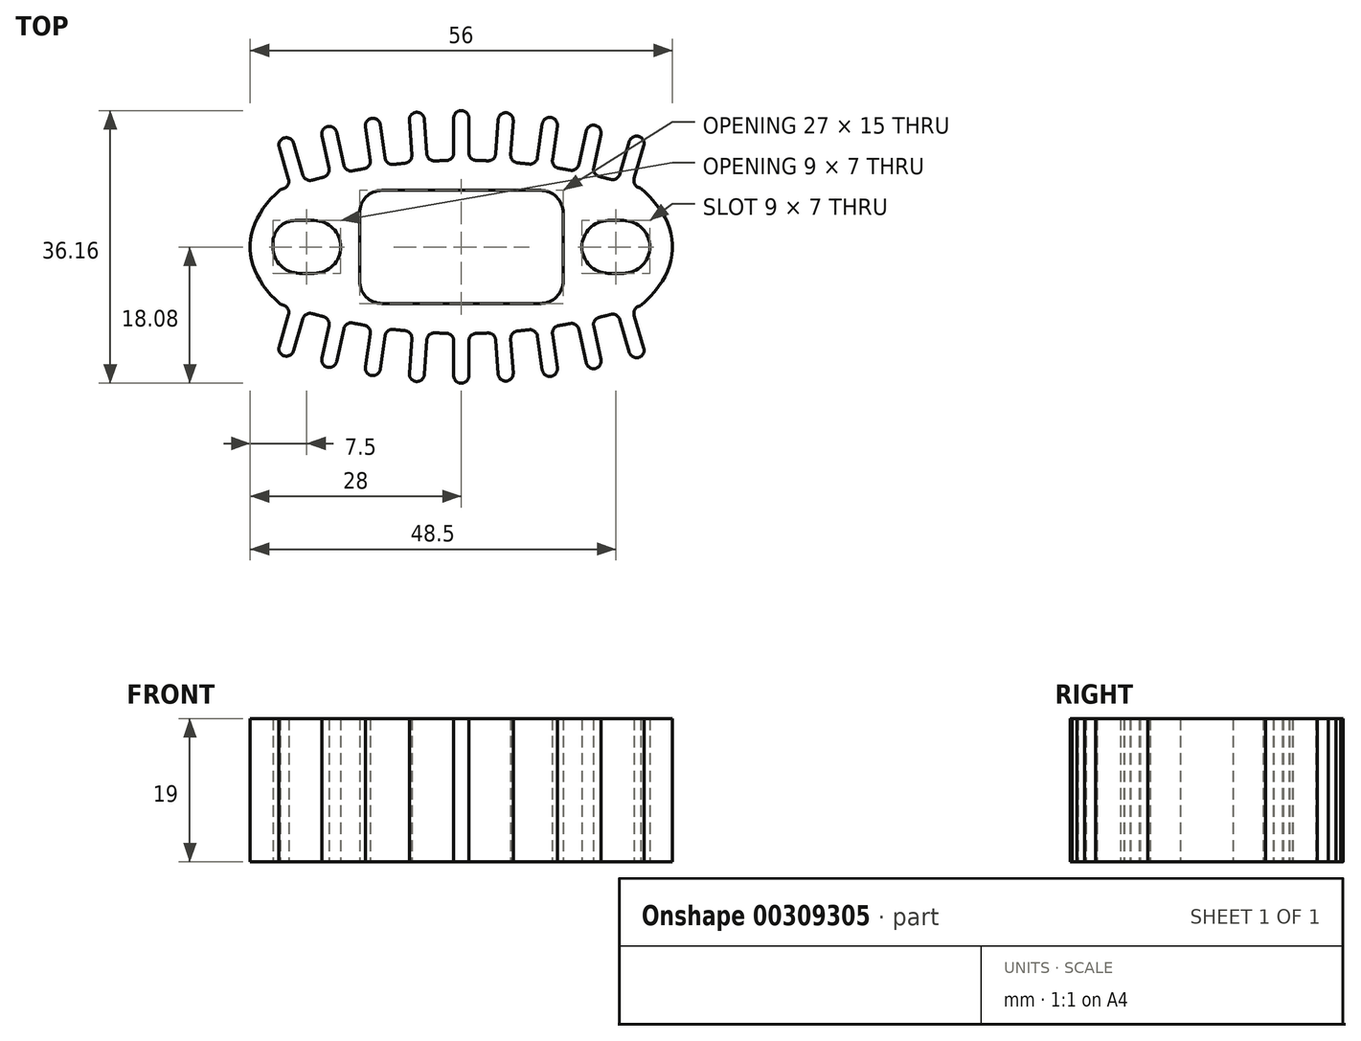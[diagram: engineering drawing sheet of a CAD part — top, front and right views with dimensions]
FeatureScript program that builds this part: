
annotation { "Feature Type Name" : "Feature", "Feature Type Description" : "" }
export const myFeature = defineFeature(function(context is Context, id is Id, definition is map)
    precondition{}
    {
        {
            var Q0;
            Q0=qCreatedBy(makeId("Top.planeOp"),FACE);
            var sketch = newSketch(context, id + "F0", { "sketchPlane" : qUnion([Q0])});
            skLineSegment(sketch, "E0.bottom", {"start": v(-10.5, 7.5) * mm, "end": v(10.5, 7.5) * mm});
            skLineSegment(sketch, "E0.top", {"start": v(-10.5, -7.5) * mm, "end": v(10.5, -7.5) * mm});
            skLineSegment(sketch, "E0.left", {"start": v(-13.5, 4.5) * mm, "end": v(-13.5, -4.5) * mm});
            skLineSegment(sketch, "E0.right", {"start": v(13.5, 4.5) * mm, "end": v(13.5, -4.5) * mm});
            skPoint(sketch, "E1.visualSharp", {"position": v(-13.5, 7.5) * mm});
            skArc(sketch, "E1.filletArc", {"start": v(-10.5, 7.5) * mm, "mid": v(-12.62, 6.62) * mm, "end": v(-13.5, 4.5) * mm});
            skPoint(sketch, "E2.visualSharp", {"position": v(-13.5, -7.5) * mm});
            skArc(sketch, "E2.filletArc", {"start": v(-13.5, -4.5) * mm, "mid": v(-12.62, -6.62) * mm, "end": v(-10.5, -7.5) * mm});
            skPoint(sketch, "E3.visualSharp", {"position": v(13.5, -7.5) * mm});
            skArc(sketch, "E3.filletArc", {"start": v(10.5, -7.5) * mm, "mid": v(12.62, -6.62) * mm, "end": v(13.5, -4.5) * mm});
            skPoint(sketch, "E4.visualSharp", {"position": v(13.5, 7.5) * mm});
            skArc(sketch, "E4.filletArc", {"start": v(13.5, 4.5) * mm, "mid": v(12.62, 6.62) * mm, "end": v(10.5, 7.5) * mm});
            skLineSegment(sketch, "E5.bottom", {"start": v(-22, 3.5) * mm, "end": v(-19.5, 3.5) * mm});
            skLineSegment(sketch, "E5.top", {"start": v(-21.5, -3.5) * mm, "end": v(-19.5, -3.5) * mm});
            skLineSegment(sketch, "E5.left", {"start": v(-25, 0.5) * mm, "end": v(-25, 0) * mm});
            skLineSegment(sketch, "E5.right", {"start": v(-16, 0) * mm, "end": v(-16, 0) * mm});
            skLineSegment(sketch, "E6.bottom", {"start": v(19.5, 3.5) * mm, "end": v(21.5, 3.5) * mm});
            skLineSegment(sketch, "E6.top", {"start": v(19.5, -3.5) * mm, "end": v(21.5, -3.5) * mm});
            skLineSegment(sketch, "E6.left", {"start": v(16, 0) * mm, "end": v(16, 0) * mm});
            skLineSegment(sketch, "E6.right", {"start": v(25, 0) * mm, "end": v(25, 0) * mm});
            skPoint(sketch, "E7.visualSharp", {"position": v(-25, 3.5) * mm});
            skArc(sketch, "E7.filletArc", {"start": v(-22, 3.5) * mm, "mid": v(-24.12, 2.62) * mm, "end": v(-25, 0.5) * mm});
            skPoint(sketch, "E8.visualSharp", {"position": v(-25, -3.5) * mm});
            skArc(sketch, "E8.filletArc", {"start": v(-25, 0) * mm, "mid": v(-23.97, -2.47) * mm, "end": v(-21.5, -3.5) * mm});
            skPoint(sketch, "E9.visualSharp", {"position": v(-16, -3.5) * mm});
            skArc(sketch, "E9.filletArc", {"start": v(-19.5, -3.5) * mm, "mid": v(-17.03, -2.47) * mm, "end": v(-16, 0) * mm});
            skPoint(sketch, "E10.visualSharp", {"position": v(-16, 3.5) * mm});
            skArc(sketch, "E10.filletArc", {"start": v(-16, 0) * mm, "mid": v(-17.03, 2.47) * mm, "end": v(-19.5, 3.5) * mm});
            skPoint(sketch, "E11.visualSharp", {"position": v(16, -3.5) * mm});
            skArc(sketch, "E11.filletArc", {"start": v(16, 0) * mm, "mid": v(17.03, -2.47) * mm, "end": v(19.5, -3.5) * mm});
            skPoint(sketch, "E12.visualSharp", {"position": v(16, 3.5) * mm});
            skArc(sketch, "E12.filletArc", {"start": v(19.5, 3.5) * mm, "mid": v(17.03, 2.47) * mm, "end": v(16, 0) * mm});
            skPoint(sketch, "E13.visualSharp", {"position": v(25, -3.5) * mm});
            skArc(sketch, "E13.filletArc", {"start": v(21.5, -3.5) * mm, "mid": v(23.97, -2.47) * mm, "end": v(25, 0) * mm});
            skPoint(sketch, "E14.visualSharp", {"position": v(25, 3.5) * mm});
            skArc(sketch, "E14.filletArc", {"start": v(25, 0) * mm, "mid": v(23.97, 2.47) * mm, "end": v(21.5, 3.5) * mm});
            skEllipticalArc(sketch, "E15", {});
            skArc(sketch, "E16", {"start": v(23.77, 7.8) * mm, "mid": v(23.68, 7.83) * mm, "end": v(23.59, 7.86) * mm});
            skLineSegment(sketch, "E17.0", {"start": v(23.52, 14.67) * mm, "end": v(23.52, 14.67) * mm});
            skEllipticalArc(sketch, "E18.trimOffspring", {});
            skPoint(sketch, "E19", {"position": v(-28, 0) * mm});
            skLineSegment(sketch, "E20.0", {"start": v(1, 12.47) * mm, "end": v(1, 17.08) * mm});
            skLineSegment(sketch, "E21.MirrorCS", {"start": v(-1, 12.46) * mm, "end": v(-1, 17.08) * mm});
            skLineSegment(sketch, "E22.1.0", {"start": v(-6.57, 12.18) * mm, "end": v(-6.9, 16.79) * mm});
            skLineSegment(sketch, "E22.1.1", {"start": v(-4.57, 12.33) * mm, "end": v(-4.9, 16.93) * mm});
            skLineSegment(sketch, "E22.2.0", {"start": v(-12.1, 11.5) * mm, "end": v(-12.73, 15.93) * mm});
            skLineSegment(sketch, "E22.2.1", {"start": v(-10.11, 11.8) * mm, "end": v(-10.75, 16.22) * mm});
            skLineSegment(sketch, "E22.3.0", {"start": v(-17.55, 10.42) * mm, "end": v(-18.5, 14.78) * mm});
            skLineSegment(sketch, "E22.3.1", {"start": v(-15.6, 10.86) * mm, "end": v(-16.55, 15.2) * mm});
            skLineSegment(sketch, "E22.4.0", {"start": v(-22.92, 8.96) * mm, "end": v(-24.17, 13.21) * mm});
            skLineSegment(sketch, "E22.4.1", {"start": v(-21, 9.54) * mm, "end": v(-22.25, 13.78) * mm});
            skLineSegment(sketch, "E22.84.0", {"start": v(21, 9.64) * mm, "end": v(22.29, 14) * mm});
            skLineSegment(sketch, "E22.84.1", {"start": v(22.93, 9.1) * mm, "end": v(24.2, 13.43) * mm});
            skLineSegment(sketch, "E22.85.0", {"start": v(15.6, 10.94) * mm, "end": v(16.56, 15.36) * mm});
            skLineSegment(sketch, "E22.85.1", {"start": v(17.55, 10.52) * mm, "end": v(18.51, 14.94) * mm});
            skLineSegment(sketch, "E22.86.0", {"start": v(10.1, 11.84) * mm, "end": v(10.75, 16.32) * mm});
            skLineSegment(sketch, "E22.86.1", {"start": v(12.08, 11.57) * mm, "end": v(12.73, 16.04) * mm});
            skLineSegment(sketch, "E22.87.0", {"start": v(4.56, 12.35) * mm, "end": v(4.88, 16.87) * mm});
            skLineSegment(sketch, "E22.87.1", {"start": v(6.55, 12.22) * mm, "end": v(6.88, 16.73) * mm});
            skLineSegment(sketch, "E23.trimOffspring", {"start": v(-11.89, 17.06) * mm, "end": v(-11.89, 17.06) * mm});
            skLineSegment(sketch, "E24.trimOffspring", {"start": v(-23.5, 14.45) * mm, "end": v(-23.5, 14.45) * mm});
            skPoint(sketch, "E25.orphan", {"position": v(-25.73, 13.75) * mm});
            skLineSegment(sketch, "E26.trimOffspring", {"start": v(-17.74, 15.96) * mm, "end": v(-17.74, 15.96) * mm});
            skLineSegment(sketch, "E27.trimOffspring", {"start": v(5.95, 17.8) * mm, "end": v(5.95, 17.8) * mm});
            skLineSegment(sketch, "E28.trimOffspring", {"start": v(11.88, 17.17) * mm, "end": v(11.88, 17.17) * mm});
            skLineSegment(sketch, "E29.trimOffspring", {"start": v(17.74, 16.13) * mm, "end": v(17.74, 16.13) * mm});
            skPoint(sketch, "E30.orphan", {"position": v(25.8, 13.97) * mm});
            skPoint(sketch, "E31.orphan", {"position": v(-4.48, 11.06) * mm});
            skPoint(sketch, "E32.orphan", {"position": v(-6.5, 11.2) * mm});
            skPoint(sketch, "E33.orphan", {"position": v(-9.93, 10.53) * mm});
            skPoint(sketch, "E34.orphan", {"position": v(-11.95, 10.54) * mm});
            skPoint(sketch, "E35.orphan", {"position": v(-15.33, 9.61) * mm});
            skPoint(sketch, "E36.orphan", {"position": v(-17.35, 9.48) * mm});
            skPoint(sketch, "E37.orphan", {"position": v(-20.65, 8.31) * mm});
            skPoint(sketch, "E38.orphan", {"position": v(-22.65, 8.03) * mm});
            skPoint(sketch, "E39.orphan", {"position": v(4.49, 11.38) * mm});
            skPoint(sketch, "E40.orphan", {"position": v(6.46, 10.94) * mm});
            skPoint(sketch, "E41.orphan", {"position": v(9.96, 10.88) * mm});
            skPoint(sketch, "E42.orphan", {"position": v(11.9, 10.3) * mm});
            skPoint(sketch, "E43.orphan", {"position": v(15.39, 9.99) * mm});
            skPoint(sketch, "E44.orphan", {"position": v(20.74, 8.71) * mm});
            skPoint(sketch, "E45.orphan", {"position": v(22.57, 7.87) * mm});
            skArc(sketch, "E46.trimOffspring", {"start": v(-23.57, 7.73) * mm, "mid": v(-23.8, 7.66) * mm, "end": v(-24.01, 7.58) * mm});
            skArc(sketch, "E47.trimOffspring", {"start": v(-18.29, 9.24) * mm, "mid": v(-19.04, 9.05) * mm, "end": v(-19.79, 8.85) * mm});
            skArc(sketch, "E48.trimOffspring", {"start": v(-12.9, 10.37) * mm, "mid": v(-13.67, 10.23) * mm, "end": v(-14.43, 10.09) * mm});
            skArc(sketch, "E49.trimOffspring", {"start": v(-7.46, 11.1) * mm, "mid": v(-8.23, 11.03) * mm, "end": v(-9, 10.94) * mm});
            skArc(sketch, "E50.trimOffspring", {"start": v(3.52, 11.42) * mm, "mid": v(2.74, 11.45) * mm, "end": v(1.97, 11.47) * mm});
            skArc(sketch, "E51.trimOffspring", {"start": v(9, 10.99) * mm, "mid": v(8.23, 11.07) * mm, "end": v(7.46, 11.15) * mm});
            skArc(sketch, "E52.trimOffspring", {"start": v(19.8, 8.96) * mm, "mid": v(19.05, 9.15) * mm, "end": v(18.3, 9.34) * mm});
            skPoint(sketch, "E53.orphan", {"position": v(17.28, 9.27) * mm});
            skArc(sketch, "E54.trimOffspring", {"start": v(14.43, 10.17) * mm, "mid": v(13.67, 10.3) * mm, "end": v(12.9, 10.44) * mm});
            skPoint(sketch, "E55.orphan", {"position": v(1, 11.2) * mm});
            skPoint(sketch, "E56.orphan", {"position": v(-1, 11.5) * mm});
            skArc(sketch, "E57.trimOffspring", {"start": v(-1.98, 11.46) * mm, "mid": v(-2.75, 11.44) * mm, "end": v(-3.53, 11.4) * mm});
            skPoint(sketch, "E58.orphan", {"position": v(0, 11.5) * mm});
            skPoint(sketch, "E59.newPointA", {"position": v(-24.55, 14.5) * mm});
            skArc(sketch, "E59.filletArc", {"start": v(-23.5, 14.45) * mm, "mid": v(-24.1, 13.97) * mm, "end": v(-24.17, 13.21) * mm});
            skPoint(sketch, "E60.newPointB", {"position": v(-22.55, 14.79) * mm});
            skArc(sketch, "E60.filletArc", {"start": v(-22.25, 13.78) * mm, "mid": v(-22.74, 14.37) * mm, "end": v(-23.5, 14.45) * mm});
            skPoint(sketch, "E61.newPointA", {"position": v(-18.78, 16.07) * mm});
            skArc(sketch, "E61.filletArc", {"start": v(-17.74, 15.96) * mm, "mid": v(-18.37, 15.53) * mm, "end": v(-18.5, 14.78) * mm});
            skPoint(sketch, "E62.newPointA", {"position": v(-16.76, 16.2) * mm});
            skArc(sketch, "E62.filletArc", {"start": v(-16.55, 15.2) * mm, "mid": v(-16.98, 15.83) * mm, "end": v(-17.74, 15.96) * mm});
            skPoint(sketch, "E63.newPointA", {"position": v(-12.91, 17.22) * mm});
            skArc(sketch, "E63.filletArc", {"start": v(-11.89, 17.06) * mm, "mid": v(-12.54, 16.67) * mm, "end": v(-12.73, 15.93) * mm});
            skPoint(sketch, "E64.newPointA", {"position": v(-10.9, 17.2) * mm});
            skArc(sketch, "E64.filletArc", {"start": v(-10.75, 16.22) * mm, "mid": v(-11.14, 16.88) * mm, "end": v(-11.89, 17.06) * mm});
            skPoint(sketch, "E65.newPointA", {"position": v(4.97, 18.11) * mm});
            skArc(sketch, "E65.filletArc", {"start": v(5.95, 17.8) * mm, "mid": v(5.22, 17.55) * mm, "end": v(4.88, 16.87) * mm});
            skPoint(sketch, "E66.newPointA", {"position": v(6.94, 17.68) * mm});
            skArc(sketch, "E66.filletArc", {"start": v(6.88, 16.73) * mm, "mid": v(6.63, 17.45) * mm, "end": v(5.95, 17.8) * mm});
            skPoint(sketch, "E67.newPointA", {"position": v(10.92, 17.56) * mm});
            skArc(sketch, "E67.filletArc", {"start": v(11.88, 17.17) * mm, "mid": v(11.14, 16.98) * mm, "end": v(10.75, 16.32) * mm});
            skPoint(sketch, "E68.newPointA", {"position": v(12.86, 16.98) * mm});
            skArc(sketch, "E68.filletArc", {"start": v(12.73, 16.04) * mm, "mid": v(12.54, 16.78) * mm, "end": v(11.88, 17.17) * mm});
            skPoint(sketch, "E69.newPointA", {"position": v(16.82, 16.59) * mm});
            skArc(sketch, "E69.filletArc", {"start": v(17.74, 16.13) * mm, "mid": v(17, 16) * mm, "end": v(16.56, 15.36) * mm});
            skPoint(sketch, "E70.newPointA", {"position": v(18.71, 15.87) * mm});
            skArc(sketch, "E70.filletArc", {"start": v(18.51, 14.94) * mm, "mid": v(18.38, 15.7) * mm, "end": v(17.74, 16.13) * mm});
            skPoint(sketch, "E71.newPointA", {"position": v(22.64, 15.2) * mm});
            skArc(sketch, "E71.filletArc", {"start": v(23.52, 14.67) * mm, "mid": v(22.76, 14.59) * mm, "end": v(22.29, 14) * mm});
            skPoint(sketch, "E72.newPointA", {"position": v(24.47, 14.34) * mm});
            skArc(sketch, "E72.filletArc", {"start": v(24.2, 13.43) * mm, "mid": v(24.12, 14.19) * mm, "end": v(23.52, 14.67) * mm});
            skLineSegment(sketch, "E73", {"start": v(-5.82, 17.85) * mm, "end": v(-5.82, 17.85) * mm});
            skLineSegment(sketch, "E74", {"start": v(0.14, 18.07) * mm, "end": v(0.14, 18.07) * mm});
            skPoint(sketch, "E75.visualSharp", {"position": v(-6.98, 17.94) * mm});
            skArc(sketch, "E75.filletArc", {"start": v(-5.82, 17.85) * mm, "mid": v(-6.6, 17.57) * mm, "end": v(-6.9, 16.79) * mm});
            skPoint(sketch, "E76.visualSharp", {"position": v(-4.96, 17.79) * mm});
            skArc(sketch, "E76.filletArc", {"start": v(-4.9, 16.93) * mm, "mid": v(-5.19, 17.56) * mm, "end": v(-5.82, 17.85) * mm});
            skPoint(sketch, "E77.visualSharp", {"position": v(-1, 18.24) * mm});
            skArc(sketch, "E77.filletArc", {"start": v(0.14, 18.07) * mm, "mid": v(-0.66, 17.84) * mm, "end": v(-1, 17.08) * mm});
            skPoint(sketch, "E78.visualSharp", {"position": v(1, 17.95) * mm});
            skArc(sketch, "E78.filletArc", {"start": v(1, 17.08) * mm, "mid": v(0.75, 17.74) * mm, "end": v(0.14, 18.07) * mm});
            skPoint(sketch, "E79.visualSharp", {"position": v(1, 11.49) * mm});
            skArc(sketch, "E79.filletArc", {"start": v(1, 12.47) * mm, "mid": v(1.28, 11.77) * mm, "end": v(1.97, 11.47) * mm});
            skPoint(sketch, "E80.visualSharp", {"position": v(4.49, 11.37) * mm});
            skArc(sketch, "E80.filletArc", {"start": v(3.52, 11.42) * mm, "mid": v(4.23, 11.67) * mm, "end": v(4.56, 12.35) * mm});
            skPoint(sketch, "E81.visualSharp", {"position": v(6.48, 11.24) * mm});
            skArc(sketch, "E81.filletArc", {"start": v(6.55, 12.22) * mm, "mid": v(6.79, 11.5) * mm, "end": v(7.46, 11.15) * mm});
            skPoint(sketch, "E82.visualSharp", {"position": v(9.96, 10.87) * mm});
            skArc(sketch, "E82.filletArc", {"start": v(9, 10.99) * mm, "mid": v(9.72, 11.2) * mm, "end": v(10.1, 11.84) * mm});
            skPoint(sketch, "E83.visualSharp", {"position": v(11.94, 10.6) * mm});
            skArc(sketch, "E83.filletArc", {"start": v(12.08, 11.57) * mm, "mid": v(12.27, 10.83) * mm, "end": v(12.9, 10.44) * mm});
            skPoint(sketch, "E84.visualSharp", {"position": v(15.39, 9.98) * mm});
            skArc(sketch, "E84.filletArc", {"start": v(14.43, 10.17) * mm, "mid": v(15.17, 10.32) * mm, "end": v(15.6, 10.94) * mm});
            skPoint(sketch, "E85.visualSharp", {"position": v(17.34, 9.56) * mm});
            skArc(sketch, "E85.filletArc", {"start": v(17.55, 10.52) * mm, "mid": v(17.68, 9.78) * mm, "end": v(18.3, 9.34) * mm});
            skPoint(sketch, "E86.visualSharp", {"position": v(20.73, 8.7) * mm});
            skArc(sketch, "E86.filletArc", {"start": v(19.8, 8.96) * mm, "mid": v(20.54, 9.05) * mm, "end": v(21, 9.64) * mm});
            skPoint(sketch, "E87.visualSharp", {"position": v(22.65, 8.15) * mm});
            skArc(sketch, "E87.filletArc", {"start": v(22.93, 9.1) * mm, "mid": v(23, 8.34) * mm, "end": v(23.59, 7.86) * mm});
            skPoint(sketch, "E88.visualSharp", {"position": v(-1, 11.48) * mm});
            skArc(sketch, "E88.filletArc", {"start": v(-1.98, 11.46) * mm, "mid": v(-1.29, 11.76) * mm, "end": v(-1, 12.46) * mm});
            skPoint(sketch, "E89.visualSharp", {"position": v(-4.5, 11.35) * mm});
            skArc(sketch, "E89.filletArc", {"start": v(-4.57, 12.33) * mm, "mid": v(-4.24, 11.65) * mm, "end": v(-3.53, 11.4) * mm});
            skArc(sketch, "E90.filletArc", {"start": v(-7.46, 11.1) * mm, "mid": v(-6.8, 11.46) * mm, "end": v(-6.57, 12.18) * mm});
            skPoint(sketch, "E91.visualSharp", {"position": v(-9.97, 10.82) * mm});
            skArc(sketch, "E91.filletArc", {"start": v(-10.11, 11.8) * mm, "mid": v(-9.73, 11.14) * mm, "end": v(-9, 10.94) * mm});
            skPoint(sketch, "E92.visualSharp", {"position": v(-11.95, 10.53) * mm});
            skArc(sketch, "E92.filletArc", {"start": v(-12.9, 10.37) * mm, "mid": v(-12.27, 10.77) * mm, "end": v(-12.1, 11.5) * mm});
            skPoint(sketch, "E93.visualSharp", {"position": v(-15.4, 9.9) * mm});
            skArc(sketch, "E93.filletArc", {"start": v(-15.6, 10.86) * mm, "mid": v(-15.17, 10.24) * mm, "end": v(-14.43, 10.09) * mm});
            skPoint(sketch, "E94.visualSharp", {"position": v(-17.34, 9.47) * mm});
            skArc(sketch, "E94.filletArc", {"start": v(-18.29, 9.24) * mm, "mid": v(-17.68, 9.68) * mm, "end": v(-17.55, 10.42) * mm});
            skPoint(sketch, "E95.visualSharp", {"position": v(-20.73, 8.6) * mm});
            skArc(sketch, "E95.filletArc", {"start": v(-21, 9.54) * mm, "mid": v(-20.54, 8.95) * mm, "end": v(-19.79, 8.85) * mm});
            skPoint(sketch, "E96.visualSharp", {"position": v(-22.65, 8.02) * mm});
            skArc(sketch, "E96.filletArc", {"start": v(-23.57, 7.73) * mm, "mid": v(-23, 8.21) * mm, "end": v(-22.92, 8.96) * mm});
            skArc(sketch, "E97.MirrorCS", {"start": v(23.77, -7.8) * mm, "mid": v(23.68, -7.83) * mm, "end": v(23.59, -7.86) * mm});
            skArc(sketch, "E98.MirrorCS", {"start": v(1, -12.47) * mm, "mid": v(1.28, -11.77) * mm, "end": v(1.97, -11.47) * mm});
            skArc(sketch, "E99.MirrorCS", {"start": v(-17.74, -15.96) * mm, "mid": v(-18.37, -15.53) * mm, "end": v(-18.5, -14.78) * mm});
            skArc(sketch, "E100.MirrorCS", {"start": v(-21, -9.54) * mm, "mid": v(-20.54, -8.95) * mm, "end": v(-19.79, -8.85) * mm});
            skArc(sketch, "E101.MirrorCS", {"start": v(-23.57, -7.73) * mm, "mid": v(-23.8, -7.66) * mm, "end": v(-24.01, -7.58) * mm});
            skArc(sketch, "E102.MirrorCS", {"start": v(14.43, -10.17) * mm, "mid": v(15.17, -10.32) * mm, "end": v(15.6, -10.94) * mm});
            skArc(sketch, "E103.MirrorCS", {"start": v(6.88, -16.73) * mm, "mid": v(6.63, -17.45) * mm, "end": v(5.95, -17.8) * mm});
            skArc(sketch, "E104.MirrorCS", {"start": v(-7.46, -11.1) * mm, "mid": v(-8.23, -11.03) * mm, "end": v(-9, -10.94) * mm});
            skArc(sketch, "E105.MirrorCS", {"start": v(17.74, -16.13) * mm, "mid": v(17, -16) * mm, "end": v(16.56, -15.36) * mm});
            skArc(sketch, "E106.MirrorCS", {"start": v(1, -17.08) * mm, "mid": v(0.75, -17.74) * mm, "end": v(0.14, -18.07) * mm});
            skArc(sketch, "E107.MirrorCS", {"start": v(9, -10.99) * mm, "mid": v(9.72, -11.2) * mm, "end": v(10.1, -11.84) * mm});
            skArc(sketch, "E108.MirrorCS", {"start": v(19.8, -8.96) * mm, "mid": v(19.05, -9.15) * mm, "end": v(18.3, -9.34) * mm});
            skArc(sketch, "E109.MirrorCS", {"start": v(22.93, -9.1) * mm, "mid": v(23, -8.34) * mm, "end": v(23.59, -7.86) * mm});
            skArc(sketch, "E110.MirrorCS", {"start": v(-10.75, -16.22) * mm, "mid": v(-11.14, -16.88) * mm, "end": v(-11.89, -17.06) * mm});
            skArc(sketch, "E111.MirrorCS", {"start": v(12.08, -11.57) * mm, "mid": v(12.27, -10.83) * mm, "end": v(12.9, -10.44) * mm});
            skArc(sketch, "E112.MirrorCS", {"start": v(5.95, -17.8) * mm, "mid": v(5.22, -17.55) * mm, "end": v(4.88, -16.87) * mm});
            skArc(sketch, "E113.MirrorCS", {"start": v(-23.5, -14.45) * mm, "mid": v(-24.1, -13.97) * mm, "end": v(-24.17, -13.21) * mm});
            skArc(sketch, "E114.MirrorCS", {"start": v(-7.46, -11.1) * mm, "mid": v(-6.8, -11.46) * mm, "end": v(-6.57, -12.18) * mm});
            skArc(sketch, "E115.MirrorCS", {"start": v(-1.98, -11.46) * mm, "mid": v(-1.29, -11.76) * mm, "end": v(-1, -12.46) * mm});
            skArc(sketch, "E116.MirrorCS", {"start": v(-12.9, -10.37) * mm, "mid": v(-13.67, -10.23) * mm, "end": v(-14.43, -10.09) * mm});
            skArc(sketch, "E117.MirrorCS", {"start": v(19.8, -8.96) * mm, "mid": v(20.54, -9.05) * mm, "end": v(21, -9.64) * mm});
            skArc(sketch, "E118.MirrorCS", {"start": v(12.73, -16.04) * mm, "mid": v(12.54, -16.78) * mm, "end": v(11.88, -17.17) * mm});
            skArc(sketch, "E119.MirrorCS", {"start": v(18.51, -14.94) * mm, "mid": v(18.38, -15.7) * mm, "end": v(17.74, -16.13) * mm});
            skArc(sketch, "E120.MirrorCS", {"start": v(3.52, -11.42) * mm, "mid": v(2.74, -11.45) * mm, "end": v(1.97, -11.47) * mm});
            skArc(sketch, "E121.MirrorCS", {"start": v(24.2, -13.43) * mm, "mid": v(24.12, -14.19) * mm, "end": v(23.52, -14.67) * mm});
            skArc(sketch, "E122.MirrorCS", {"start": v(-18.29, -9.24) * mm, "mid": v(-19.04, -9.05) * mm, "end": v(-19.79, -8.85) * mm});
            skArc(sketch, "E123.MirrorCS", {"start": v(-15.6, -10.86) * mm, "mid": v(-15.17, -10.24) * mm, "end": v(-14.43, -10.09) * mm});
            skArc(sketch, "E124.MirrorCS", {"start": v(-4.9, -16.93) * mm, "mid": v(-5.19, -17.56) * mm, "end": v(-5.82, -17.85) * mm});
            skArc(sketch, "E125.MirrorCS", {"start": v(17.55, -10.52) * mm, "mid": v(17.68, -9.78) * mm, "end": v(18.3, -9.34) * mm});
            skArc(sketch, "E126.MirrorCS", {"start": v(9, -10.99) * mm, "mid": v(8.23, -11.07) * mm, "end": v(7.46, -11.15) * mm});
            skArc(sketch, "E127.MirrorCS", {"start": v(-18.29, -9.24) * mm, "mid": v(-17.68, -9.68) * mm, "end": v(-17.55, -10.42) * mm});
            skArc(sketch, "E128.MirrorCS", {"start": v(-22.25, -13.78) * mm, "mid": v(-22.74, -14.37) * mm, "end": v(-23.5, -14.45) * mm});
            skArc(sketch, "E129.MirrorCS", {"start": v(-10.11, -11.8) * mm, "mid": v(-9.73, -11.14) * mm, "end": v(-9, -10.94) * mm});
            skArc(sketch, "E130.MirrorCS", {"start": v(-23.57, -7.73) * mm, "mid": v(-23, -8.21) * mm, "end": v(-22.92, -8.96) * mm});
            skArc(sketch, "E131.MirrorCS", {"start": v(-11.89, -17.06) * mm, "mid": v(-12.54, -16.67) * mm, "end": v(-12.73, -15.93) * mm});
            skArc(sketch, "E132.MirrorCS", {"start": v(14.43, -10.17) * mm, "mid": v(13.67, -10.3) * mm, "end": v(12.9, -10.44) * mm});
            skArc(sketch, "E133.MirrorCS", {"start": v(-12.9, -10.37) * mm, "mid": v(-12.27, -10.77) * mm, "end": v(-12.1, -11.5) * mm});
            skArc(sketch, "E134.MirrorCS", {"start": v(6.55, -12.22) * mm, "mid": v(6.79, -11.5) * mm, "end": v(7.46, -11.15) * mm});
            skArc(sketch, "E135.MirrorCS", {"start": v(-5.82, -17.85) * mm, "mid": v(-6.6, -17.57) * mm, "end": v(-6.9, -16.79) * mm});
            skArc(sketch, "E136.MirrorCS", {"start": v(-4.57, -12.33) * mm, "mid": v(-4.24, -11.65) * mm, "end": v(-3.53, -11.4) * mm});
            skArc(sketch, "E137.MirrorCS", {"start": v(11.88, -17.17) * mm, "mid": v(11.14, -16.98) * mm, "end": v(10.75, -16.32) * mm});
            skArc(sketch, "E138.MirrorCS", {"start": v(3.52, -11.42) * mm, "mid": v(4.23, -11.67) * mm, "end": v(4.56, -12.35) * mm});
            skArc(sketch, "E139.MirrorCS", {"start": v(-1.98, -11.46) * mm, "mid": v(-2.75, -11.44) * mm, "end": v(-3.53, -11.4) * mm});
            skArc(sketch, "E140.MirrorCS", {"start": v(23.52, -14.67) * mm, "mid": v(22.76, -14.59) * mm, "end": v(22.29, -14) * mm});
            skPoint(sketch, "E141.MirrorP", {"position": v(-15.4, -9.9) * mm});
            skPoint(sketch, "E142.MirrorP", {"position": v(4.49, -11.38) * mm});
            skPoint(sketch, "E143.MirrorP", {"position": v(11.94, -10.6) * mm});
            skPoint(sketch, "E144.MirrorP", {"position": v(1, -11.2) * mm});
            skPoint(sketch, "E145.MirrorP", {"position": v(-9.97, -10.82) * mm});
            skPoint(sketch, "E146.MirrorP", {"position": v(0, -11.5) * mm});
            skPoint(sketch, "E147.MirrorP", {"position": v(-17.34, -9.47) * mm});
            skPoint(sketch, "E148.MirrorP", {"position": v(-20.73, -8.6) * mm});
            skPoint(sketch, "E149.MirrorP", {"position": v(-4.48, -11.06) * mm});
            skPoint(sketch, "E150.MirrorP", {"position": v(6.46, -10.94) * mm});
            skArc(sketch, "E151.MirrorCS", {"start": v(0.14, -18.07) * mm, "mid": v(-0.66, -17.84) * mm, "end": v(-1, -17.08) * mm});
            skPoint(sketch, "E152.MirrorP", {"position": v(17.34, -9.56) * mm});
            skPoint(sketch, "E153.MirrorP", {"position": v(-1, -11.5) * mm});
            skPoint(sketch, "E154.MirrorP", {"position": v(15.39, -9.98) * mm});
            skPoint(sketch, "E155.MirrorP", {"position": v(20.74, -8.71) * mm});
            skArc(sketch, "E156.MirrorCS", {"start": v(-16.55, -15.2) * mm, "mid": v(-16.98, -15.83) * mm, "end": v(-17.74, -15.96) * mm});
            skPoint(sketch, "E157.MirrorP", {"position": v(-11.95, -10.53) * mm});
            skPoint(sketch, "E158.MirrorP", {"position": v(22.57, -7.87) * mm});
            skPoint(sketch, "E159.MirrorP", {"position": v(9.96, -10.88) * mm});
            skPoint(sketch, "E160.MirrorP", {"position": v(-22.65, -8.03) * mm});
            skPoint(sketch, "E161.MirrorP", {"position": v(-22.65, -8.02) * mm});
            skPoint(sketch, "E162.MirrorP", {"position": v(-1, -11.48) * mm});
            skPoint(sketch, "E163.MirrorP", {"position": v(4.49, -11.37) * mm});
            skPoint(sketch, "E164.MirrorP", {"position": v(18.71, -15.87) * mm});
            skLineSegment(sketch, "E165.MirrorCS", {"start": v(17.55, -10.52) * mm, "end": v(18.51, -14.94) * mm});
            skLineSegment(sketch, "E166.MirrorCS", {"start": v(-6.57, -12.18) * mm, "end": v(-6.9, -16.79) * mm});
            skPoint(sketch, "E167.MirrorP", {"position": v(-17.35, -9.48) * mm});
            skLineSegment(sketch, "E168.MirrorCS", {"start": v(4.56, -12.35) * mm, "end": v(4.88, -16.87) * mm});
            skLineSegment(sketch, "E169.MirrorCS", {"start": v(1, -12.47) * mm, "end": v(1, -17.08) * mm});
            skLineSegment(sketch, "E170.MirrorCS", {"start": v(-10.11, -11.8) * mm, "end": v(-10.75, -16.22) * mm});
            skPoint(sketch, "E171.MirrorP", {"position": v(20.73, -8.7) * mm});
            skLineSegment(sketch, "E172.MirrorCS", {"start": v(0.14, -18.07) * mm, "end": v(0.14, -18.07) * mm});
            skPoint(sketch, "E173.MirrorP", {"position": v(25.8, -13.97) * mm});
            skPoint(sketch, "E174.MirrorP", {"position": v(-6.5, -11.2) * mm});
            skPoint(sketch, "E175.MirrorP", {"position": v(-6.98, -17.94) * mm});
            skPoint(sketch, "E176.MirrorP", {"position": v(4.97, -18.11) * mm});
            skPoint(sketch, "E177.MirrorP", {"position": v(9.96, -10.87) * mm});
            skPoint(sketch, "E178.MirrorP", {"position": v(24.47, -14.34) * mm});
            skPoint(sketch, "E179.MirrorP", {"position": v(-10.9, -17.2) * mm});
            skPoint(sketch, "E180.MirrorP", {"position": v(17.28, -9.27) * mm});
            skLineSegment(sketch, "E181.MirrorCS", {"start": v(6.55, -12.22) * mm, "end": v(6.88, -16.73) * mm});
            skLineSegment(sketch, "E182.MirrorCS", {"start": v(-1, -12.46) * mm, "end": v(-1, -17.08) * mm});
            skLineSegment(sketch, "E183.MirrorCS", {"start": v(-15.6, -10.86) * mm, "end": v(-16.55, -15.2) * mm});
            skPoint(sketch, "E184.MirrorP", {"position": v(11.9, -10.3) * mm});
            skPoint(sketch, "E185.MirrorP", {"position": v(-20.65, -8.31) * mm});
            skLineSegment(sketch, "E186.MirrorCS", {"start": v(-22.92, -8.96) * mm, "end": v(-24.17, -13.21) * mm});
            skPoint(sketch, "E187.MirrorP", {"position": v(10.92, -17.56) * mm});
            skPoint(sketch, "E188.MirrorP", {"position": v(1, -11.49) * mm});
            skPoint(sketch, "E189.MirrorP", {"position": v(22.65, -8.15) * mm});
            skLineSegment(sketch, "E190.MirrorCS", {"start": v(-12.1, -11.5) * mm, "end": v(-12.73, -15.93) * mm});
            skPoint(sketch, "E191.MirrorP", {"position": v(16.82, -16.59) * mm});
            skLineSegment(sketch, "E192.MirrorCS", {"start": v(22.93, -9.1) * mm, "end": v(24.2, -13.43) * mm});
            skLineSegment(sketch, "E193.MirrorCS", {"start": v(-17.55, -10.42) * mm, "end": v(-18.5, -14.78) * mm});
            skPoint(sketch, "E194.MirrorP", {"position": v(-18.78, -16.07) * mm});
            skPoint(sketch, "E195.MirrorP", {"position": v(-4.96, -17.79) * mm});
            skPoint(sketch, "E196.MirrorP", {"position": v(-9.93, -10.53) * mm});
            skPoint(sketch, "E197.MirrorP", {"position": v(-16.76, -16.2) * mm});
            skPoint(sketch, "E198.MirrorP", {"position": v(6.94, -17.68) * mm});
            skLineSegment(sketch, "E199.MirrorCS", {"start": v(-4.57, -12.33) * mm, "end": v(-4.9, -16.93) * mm});
            skPoint(sketch, "E200.MirrorP", {"position": v(-22.55, -14.79) * mm});
            skLineSegment(sketch, "E201.MirrorCS", {"start": v(15.6, -10.94) * mm, "end": v(16.56, -15.36) * mm});
            skPoint(sketch, "E202.MirrorP", {"position": v(22.64, -15.2) * mm});
            skPoint(sketch, "E203.MirrorP", {"position": v(6.48, -11.24) * mm});
            skPoint(sketch, "E204.MirrorP", {"position": v(-15.33, -9.61) * mm});
            skLineSegment(sketch, "E205.MirrorCS", {"start": v(-21, -9.54) * mm, "end": v(-22.25, -13.78) * mm});
            skLineSegment(sketch, "E206.MirrorCS", {"start": v(12.08, -11.57) * mm, "end": v(12.73, -16.04) * mm});
            skPoint(sketch, "E207.MirrorP", {"position": v(-12.91, -17.22) * mm});
            skLineSegment(sketch, "E208.MirrorCS", {"start": v(-5.82, -17.85) * mm, "end": v(-5.82, -17.85) * mm});
            skPoint(sketch, "E209.MirrorP", {"position": v(-11.95, -10.54) * mm});
            skPoint(sketch, "E210.MirrorP", {"position": v(-4.5, -11.35) * mm});
            skLineSegment(sketch, "E211.MirrorCS", {"start": v(10.1, -11.84) * mm, "end": v(10.75, -16.32) * mm});
            skPoint(sketch, "E212.MirrorP", {"position": v(12.86, -16.98) * mm});
            skPoint(sketch, "E213.MirrorP", {"position": v(1, -17.95) * mm});
            skPoint(sketch, "E214.MirrorP", {"position": v(-24.55, -14.5) * mm});
            skPoint(sketch, "E215.MirrorP", {"position": v(-25.73, -13.75) * mm});
            skPoint(sketch, "E216.MirrorP", {"position": v(15.39, -9.99) * mm});
            skPoint(sketch, "E217.MirrorP", {"position": v(-1, -18.24) * mm});
            skLineSegment(sketch, "E218.MirrorCS", {"start": v(21, -9.64) * mm, "end": v(22.29, -14) * mm});
            const initialGuessF0  = {"E15": [0, 0, -1, 0, 0.028, 0.01475, 5.743103859391178, 0.5400814477884083], "E18.trimOffspring": [0, 0, -1, 0, 0.028, 0.01475, 2.5844994751126067, 3.6986858320669795]};
            skSetInitialGuess(sketch, initialGuessF0);
            skSolve(sketch);
        }
        {
            var Q0;
            Q0=makeQuery(id+"F0.imprint","IMPRINT",FACE,{"disambiguationData":[TD([[makeQuery(id+"F0.imprint","IMPRINT",EDGE,{"derivedFrom":sQuery(id+"F0.wireOp",EDGE,"E0.bottom")}),1.0]])]});
            extrude(context, id + "F1", {"entities" : qUnion([Q0]), "depth" : 19 * mm});
        }
    });
